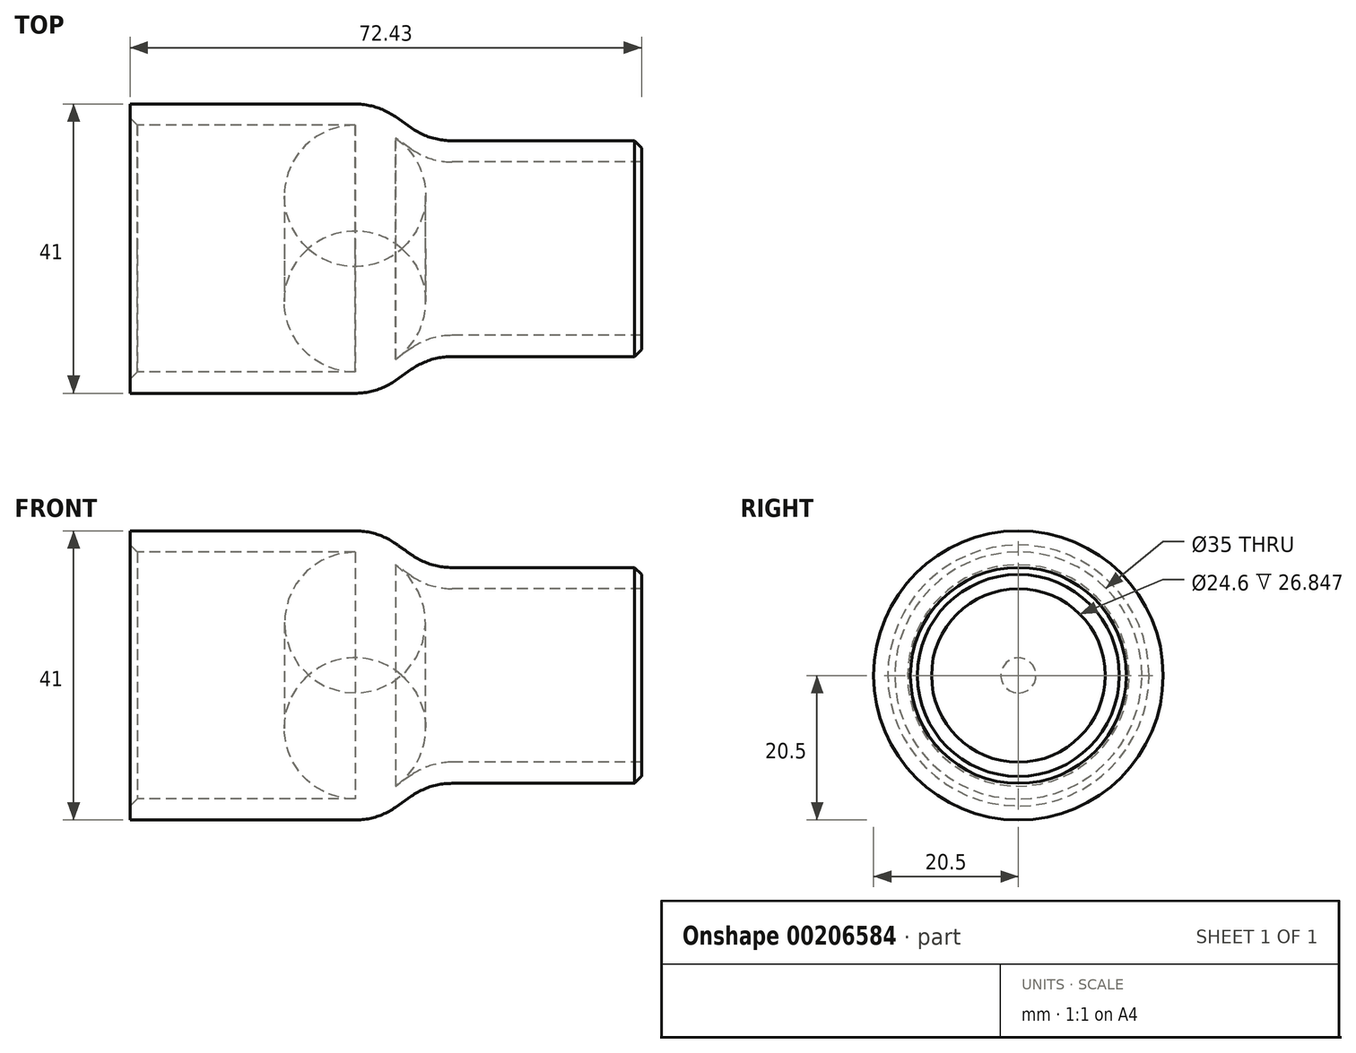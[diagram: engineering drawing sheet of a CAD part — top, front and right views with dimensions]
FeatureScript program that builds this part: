
annotation { "Feature Type Name" : "Feature", "Feature Type Description" : "" }
export const myFeature = defineFeature(function(context is Context, id is Id, definition is map)
    precondition{}
    {
        {
            var Q0;
            Q0=qCreatedBy(makeId("Front.planeOp"),FACE);
            var sketch = newSketch(context, id + "F0", { "sketchPlane" : qUnion([Q0])});
            skLineSegment(sketch, "E0", {"start": v(0, 20.5) * mm, "end": v(35, 20.5) * mm});
            skLineSegment(sketch, "E1", {"start": v(35, 20.5) * mm, "end": v(42.43, 15.3) * mm});
            skLineSegment(sketch, "E2", {"start": v(42.43, 15.3) * mm, "end": v(72.43, 15.3) * mm});
            skLineSegment(sketch, "E3", {"start": v(72.43, 15.3) * mm, "end": v(72.43, 12.3) * mm});
            skLineSegment(sketch, "E4", {"start": v(72.43, 12.3) * mm, "end": v(42.43, 12.3) * mm});
            skLineSegment(sketch, "E5", {"start": v(42.43, 12.3) * mm, "end": v(35, 17.5) * mm});
            skLineSegment(sketch, "E6", {"start": v(35, 17.5) * mm, "end": v(0, 17.5) * mm});
            skLineSegment(sketch, "E7", {"start": v(0, 17.5) * mm, "end": v(0, 20.5) * mm});
            skLineSegment(sketch, "E8", {"start": v(35, 17.5) * mm, "end": v(72.43, 17.5) * mm, "construction": true});
            skLineSegment(sketch, "E9", {"start": v(0, 0) * mm, "end": v(72.43, 0) * mm, "construction": true});
            skSolve(sketch);
        }
        {
            var Q0;
            Q0 = qSketchRegion(id + "F0", true);
            var Q1;
            Q1=sQuery(id+"F0.wireOp",EDGE,"E9");
            revolve(context, id + "F1", {"entities" : qUnion([Q0]), "axis" : qUnion([Q1]), "revolveType" : RevolveType.FULL});
        }
        {
            var Q0;
            Q0=makeQuery(id+"F1.opRevolve","SWEPT_EDGE",EDGE,{"disambiguationData":[OSD([sQuery(id+"F0.wireOp",EDGE,"E6"),sQuery(id+"F0.wireOp",EDGE,"E7")])]});
            var Q1;
            Q1=makeQuery(id+"F1.opRevolve","SWEPT_EDGE",EDGE,{"disambiguationData":[OSD([sQuery(id+"F0.wireOp",EDGE,"E2"),sQuery(id+"F0.wireOp",EDGE,"E3")])]});
            chamfer(context, id + "F2", {"entities" : qUnion([Q0, Q1]), "width" : 1 * mm, "tangentPropagation" : true});
        }
        {
            var Q0;
            Q0=makeQuery(id+"F1.opRevolve","SWEPT_EDGE",EDGE,{"disambiguationData":[OSD([sQuery(id+"F0.wireOp",EDGE,"E1"),sQuery(id+"F0.wireOp",EDGE,"E2")])]});
            var Q1;
            Q1=makeQuery(id+"F1.opRevolve","SWEPT_EDGE",EDGE,{"disambiguationData":[OSD([sQuery(id+"F0.wireOp",EDGE,"E0"),sQuery(id+"F0.wireOp",EDGE,"E1")])]});
            var Q2;
            Q2=makeQuery(id+"F1.opRevolve","SWEPT_EDGE",EDGE,{"disambiguationData":[OSD([sQuery(id+"F0.wireOp",EDGE,"E4"),sQuery(id+"F0.wireOp",EDGE,"E5")])]});
            var Q3;
            Q3=makeQuery(id+"F1.opRevolve","SWEPT_EDGE",EDGE,{"disambiguationData":[OSD([sQuery(id+"F0.wireOp",EDGE,"E5"),sQuery(id+"F0.wireOp",EDGE,"E6")])]});
            fillet(context, id + "F3", {"entities" : qUnion([Q0, Q1, Q2, Q3]), "radius" : 10 * mm, "tangentPropagation" : true, "allowEdgeOverflow" : false});
        }
    });
